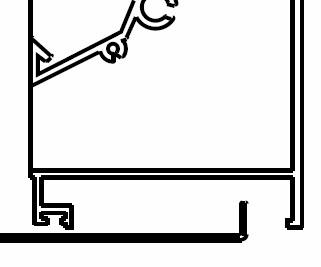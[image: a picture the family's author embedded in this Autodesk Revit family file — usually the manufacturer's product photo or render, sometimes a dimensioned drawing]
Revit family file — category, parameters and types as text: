
# Revit family: Louver_Carnes-Alum-J_Blade-Stationary-FKDC
name_source: partatom
category: Duct Accessories
revit_build: Autodesk Revit MEP 2012 (Build: 20110309_2315(x64)
units: mm (PartAtom-declared; Revit-internal decimal feet)

## types (1)
- FKDC
    04 CSI = 08 91 00
    95 CSI = 10200
    Actual Height = 24"
    Actual Width = 24"
    Assembly Code = B2010300
    Blade Material = Metal - Carnes - Steel - Galvanized
    Blade Width = 22 39/128"
    Catalog URL = http://www.carnes.com
    Default Elevation = 0"
    Depth = 4 41/256"
    Description = Extruded Aluminum Stationary J Blade Louver
    Duct Connector 1 = Duct Connection 1
    Duct Connector 2 = Duct Connection 2
    Frame Material = Metal - Carnes - Steel - Galvanized
    Height = 24"
    Manufacturer = CARNES COMPANY
    Manufacturer Fax = 608-845-6470
    Maximum Horinzontal Size = 120"W x 84"H
    Maximum System Pressure = 1.00 in-wg
    Maximum System Velocity = 812 FPM
    Maximum Vertical Size = 84"W x 120"H
    Minimum Size = 12"W x 12"H
    Model = FKDC
    Offset = 3"
    Product Line = Extruded Aluminum Stationary J Blade Louver
    Product Page URL = http://www.carnes.com
    Spec Sheet URL = http://www.carnes.com
    Subcategory = Louvers and Dampers
    URL = http://www.carnes.com
    Warranty URL = http://www.carnes.com
    Width = 24"
    ecoScorecard Product Page = http://ecoscorecard.com

## geometry (parser evidence)
native form markers: Blend x2, Sweep x7
no freeform markers — native parametric forms only
